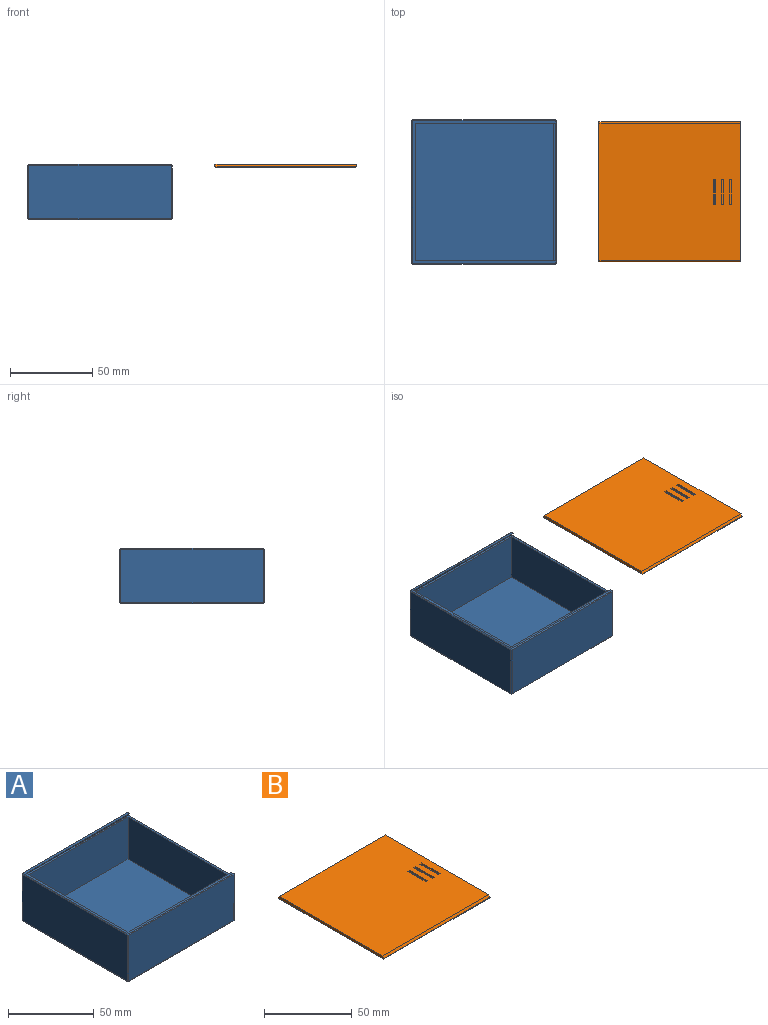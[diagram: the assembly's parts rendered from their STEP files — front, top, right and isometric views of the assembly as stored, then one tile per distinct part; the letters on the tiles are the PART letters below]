
ASSEMBLY  parts=2 mates=1
PART A: 40 faces, bbox 88x88x34 mm
  f0: plane 0.63x0.36mm, normal (1,0,0), area 0.1mm2, adj f17,f23,f24
  f1: plane 0.63x0.36mm, normal (1,0,0), area 0.1mm2, adj f18,f25,f26
  f2: plane 86.8x30.8mm, normal (1,0,0), area 2673.4mm2, adj f16,f20,f23,f26
  f3: plane 84x30mm, normal (0,1,0), area 2520mm2, adj f8,f11,f12,f13
  f4: plane 84x30mm, normal (0,-1,0), area 2520mm2, adj f8,f11,f12,f13
  f5: plane 86.8x32.8mm, normal (0,1,0), area 2847mm2, adj f22,f23,f33,f34
  f6: plane 86.8x32.8mm, normal (-1,0,0), area 2847mm2, adj f28,f33,f36,f39
  f7: plane 86.8x32.8mm, normal (0,-1,0), area 2847mm2, adj f26,f27,f35,f36
  f8: plane 86.31x32mm, normal (1,0,0), area 2690.3mm2, adj f3,f4,f9,f11,f13,f14,f15
  f9: plane 86.8x86.8mm, normal (0,0,1), area 360.6mm2, adj f8,f14,f15,f24,f25,f34,f35,f39
  f10: plane 86.8x86.8mm, normal (0,0,-1), area 7534.2mm2, adj f16,f22,f27,f28
  f11: plane 84x84mm, normal (0,0,1), area 7056mm2, adj f3,f4,f8,f12
  f12: plane 84x30mm, normal (-1,0,0), area 2520mm2, adj f3,f4,f11,f13
  f13: plane 86.31x85.4mm, normal (0,0,1), area 314.8mm2, adj f3,f4,f8,f12,f14,f15,f20
  f14: plane 85.4x2mm, normal (0,0.87,-0.5), area 197.2mm2, adj f8,f9,f13,f18
  f15: plane 85.4x2mm, normal (0,-0.87,-0.5), area 197.2mm2, adj f8,f9,f13,f17
  f16: plane 86.8x0.6mm, normal (0.71,0,-0.71), area 73.7mm2, adj f2,f10,f19,f21
  f17: plane 2.31x1.69mm, normal (0.71,-0.61,-0.35), area 1.6mm2, adj f0,f15,f20,f23,f24
  f18: plane 2.31x1.69mm, normal (0.71,0.61,-0.35), area 1.6mm2, adj f1,f14,f20,f25,f26
  f19: plane 0.6x0.6mm, normal (0.58,0.58,-0.58), area 0.3mm2, adj f16,f22,f23
  f20: plane 87.38x0.6mm, normal (0.71,0,0.71), area 73.8mm2, adj f2,f13,f17,f18,f23,f26
  f21: plane 0.6x0.6mm, normal (0.58,-0.58,-0.58), area 0.3mm2, adj f16,f26,f27
  f22: plane 86.8x0.6mm, normal (0,0.71,-0.71), area 73.7mm2, adj f5,f10,f19,f29
  f23: plane 32.8x0.6mm, normal (0.71,0.71,0), area 27.5mm2, adj f0,f2,f5,f17,f19,f20,f30
  f24: plane 1.4x0.6mm, normal (0.71,0,0.71), area 0.7mm2, adj f0,f9,f17,f30
  f25: plane 1.4x0.6mm, normal (0.71,0,0.71), area 0.7mm2, adj f1,f9,f18,f31
  f26: plane 32.8x0.6mm, normal (0.71,-0.71,0), area 27.5mm2, adj f1,f2,f7,f18,f20,f21,f31
  f27: plane 86.8x0.6mm, normal (0,-0.71,-0.71), area 73.7mm2, adj f7,f10,f21,f32
  f28: plane 86.8x0.6mm, normal (-0.71,0,-0.71), area 73.7mm2, adj f6,f10,f29,f32
  f29: plane 0.6x0.6mm, normal (-0.58,0.58,-0.58), area 0.3mm2, adj f22,f28,f33
  f30: plane 0.6x0.6mm, normal (0.58,0.58,0.58), area 0.3mm2, adj f23,f24,f34
  f31: plane 0.6x0.6mm, normal (0.58,-0.58,0.58), area 0.3mm2, adj f25,f26,f35
  f32: plane 0.6x0.6mm, normal (-0.58,-0.58,-0.58), area 0.3mm2, adj f27,f28,f36
  f33: plane 32.8x0.6mm, normal (-0.71,0.71,0), area 27.8mm2, adj f5,f6,f29,f37
  f34: plane 86.8x0.6mm, normal (0,0.71,0.71), area 73.7mm2, adj f5,f9,f30,f37
  f35: plane 86.8x0.6mm, normal (0,-0.71,0.71), area 73.7mm2, adj f7,f9,f31,f38
  f36: plane 32.8x0.6mm, normal (-0.71,-0.71,0), area 27.8mm2, adj f6,f7,f32,f38
  f37: plane 0.6x0.6mm, normal (-0.58,0.58,0.58), area 0.3mm2, adj f33,f34,f39
  f38: plane 0.6x0.6mm, normal (-0.58,-0.58,0.58), area 0.3mm2, adj f35,f36,f39
  f39: plane 86.8x0.6mm, normal (-0.71,0,0.71), area 73.7mm2, adj f6,f9,f37,f38
PART B: 25 faces, bbox 86x85.3x2 mm
  f0: plane 86x83.6mm, normal (0,0,1), area 7122.1mm2, adj f2,f3,f4,f5,f6,f7,f8,f10
  f1: plane 85.31x84.71mm, normal (0,0,-1), area 7226.3mm2, adj f21,f22,f23,f24
  f2: plane 86x1.48mm, normal (0,0.87,0.5), area 147mm2, adj f0,f4,f5,f23
  f3: plane 86x1.48mm, normal (0,-0.87,0.5), area 147mm2, adj f0,f4,f5,f22
  f4: plane 85.31x1.65mm, normal (1,0,0), area 139.8mm2, adj f0,f2,f3,f22,f23,f24
  f5: plane 85.31x1.65mm, normal (-1,0,0), area 139.8mm2, adj f0,f2,f3,f21,f22,f23
  f6: plane 1.5x1mm, normal (0,-1,0), area 1mm2, adj f0,f8,f9,f20
  f7: plane 1.5x1mm, normal (0,1,0), area 1mm2, adj f0,f8,f9,f20
  f8: plane 15x1mm, normal (-1,0,0), area 15mm2, adj f0,f6,f7,f9
  f9: plane 15x0.5mm, normal (0,0,1), area 7.5mm2, adj f6,f7,f8,f20
  f10: plane 1.5x1mm, normal (0,-1,0), area 1mm2, adj f0,f12,f13,f19
  f11: plane 1.5x1mm, normal (0,1,0), area 1mm2, adj f0,f12,f13,f19
  f12: plane 15x1mm, normal (-1,0,0), area 15mm2, adj f0,f10,f11,f13
  f13: plane 15x0.5mm, normal (0,0,1), area 7.5mm2, adj f10,f11,f12,f19
  f14: plane 1.5x1mm, normal (0,-1,0), area 1mm2, adj f0,f16,f17,f18
  f15: plane 1.5x1mm, normal (0,1,0), area 1mm2, adj f0,f16,f17,f18
  f16: plane 15x1mm, normal (-1,0,0), area 15mm2, adj f0,f14,f15,f17
  f17: plane 15x0.5mm, normal (0,0,1), area 7.5mm2, adj f14,f15,f16,f18
  f18: plane 15x1mm, normal (0.71,0,0.71), area 21.2mm2, adj f0,f14,f15,f17
  f19: plane 15x1mm, normal (0.71,0,0.71), area 21.2mm2, adj f0,f10,f11,f13
  f20: plane 15x1mm, normal (0.71,0,0.71), area 21.2mm2, adj f0,f6,f7,f9
  f21: plane 85.11x0.35mm, normal (-0.71,0,-0.71), area 41.6mm2, adj f1,f5,f22,f23
  f22: plane 86x0.52mm, normal (0,-0.87,-0.5), area 51.5mm2, adj f1,f3,f4,f5,f21,f24
  f23: plane 86x0.52mm, normal (0,0.87,-0.5), area 51.5mm2, adj f1,f2,f4,f5,f21,f24
  f24: plane 85.11x0.35mm, normal (0.71,0,-0.71), area 41.6mm2, adj f1,f4,f22,f23
PLACE A t=(-44,-44,0)mm
PLACE B t=(-19.97,-44,32)mm
MATE slider B.f5 <-> A.f8  axis (-1,0,0) through (70.03,0,34)mm
